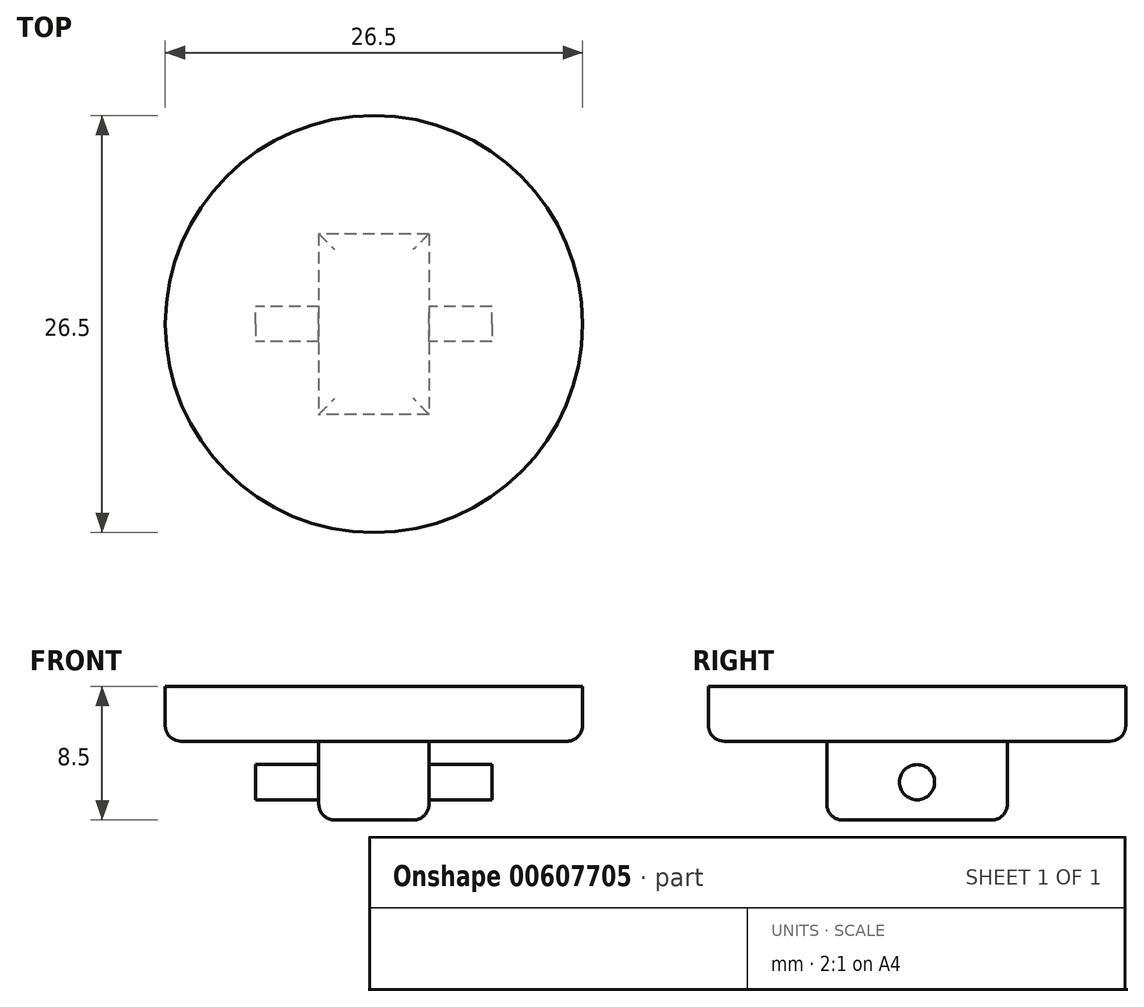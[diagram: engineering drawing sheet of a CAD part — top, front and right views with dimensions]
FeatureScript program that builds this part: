
annotation { "Feature Type Name" : "Feature", "Feature Type Description" : "" }
export const myFeature = defineFeature(function(context is Context, id is Id, definition is map)
    precondition{}
    {
        {
            var Q0;
            Q0=qCreatedBy(makeId("Top.planeOp"),FACE);
            var sketch = newSketch(context, id + "F0", { "sketchPlane" : qUnion([Q0])});
            skCircle(sketch, "E0", {"center": v(0, 0) * mm, "radius": 13.25 * mm});
            skSolve(sketch);
        }
        {
            var Q0;
            Q0=qSketchRegion(id+"F0",true);
            extrude(context, id + "F1", {"entities" : qUnion([Q0]), "depth" : 3.5 * mm, "offsetDistance" : 25 * mm});
        }
        {
            var Q0;
            Q0=makeQuery(id+"F1.opExtrude","CAP_FACE",FACE,{"disambiguationData":[OSD([sQuery(id+"F0.wireOp",EDGE,"E0")])],"isStart":true});
            var sketch = newSketch(context, id + "F2", { "sketchPlane" : qUnion([Q0])});
            skLineSegment(sketch, "E1.bottom", {"start": v(3.5, -5.73) * mm, "end": v(-3.5, -5.73) * mm});
            skLineSegment(sketch, "E1.top", {"start": v(3.5, 5.73) * mm, "end": v(-3.5, 5.73) * mm});
            skLineSegment(sketch, "E1.left", {"start": v(3.5, -5.73) * mm, "end": v(3.5, 5.73) * mm});
            skLineSegment(sketch, "E1.right", {"start": v(-3.5, -5.73) * mm, "end": v(-3.5, 5.73) * mm});
            skPoint(sketch, "E1.middle", {"position": v(0, 0) * mm});
            skSolve(sketch);
        }
        {
            var Q0;
            Q0=qSketchRegion(id+"F2",true);
            extrude(context, id + "F3", {"entities" : qUnion([Q0]), "operationType" : NewBodyOperationType.ADD, "depth" : 5 * mm, "offsetDistance" : 25 * mm});
        }
        {
            var Q0;
            Q0=qCreatedBy(makeId("Right.planeOp"),FACE);
            var sketch = newSketch(context, id + "F4", { "sketchPlane" : qUnion([Q0])});
            skCircle(sketch, "E2", {"center": v(0, -2.6) * mm, "radius": 1.12 * mm});
            skSolve(sketch);
        }
        {
            var Q0;
            Q0=qSketchRegion(id+"F4",true);
            extrude(context, id + "F5", {"entities" : qUnion([Q0]), "operationType" : NewBodyOperationType.ADD, "depth" : 15 * mm, "offsetDistance" : 25 * mm, "symmetric" : true});
        }
        {
            var Q0;
            Q0=makeQuery(id+"F1.opExtrude","CAP_EDGE",EDGE,{"disambiguationData":[OSD([sQuery(id+"F0.wireOp",EDGE,"E0")])],"isStart":true});
            fillet(context, id + "F6", {"entities" : qUnion([Q0]), "radius" : 1 * mm, "tangentPropagation" : true, "allowEdgeOverflow" : false});
        }
        {
            var Q0;
            Q0=makeQuery(id+"F3.opExtrude","CAP_FACE",FACE,{"disambiguationData":[OSD([sQuery(id+"F2.wireOp",EDGE,"E1.bottom"),sQuery(id+"F2.wireOp",EDGE,"E1.top"),sQuery(id+"F2.wireOp",EDGE,"E1.left"),sQuery(id+"F2.wireOp",EDGE,"E1.right")])],"isStart":false});
            fillet(context, id + "F7", {"entities" : qUnion([Q0]), "radius" : 1 * mm, "tangentPropagation" : true, "allowEdgeOverflow" : false});
        }
    });
